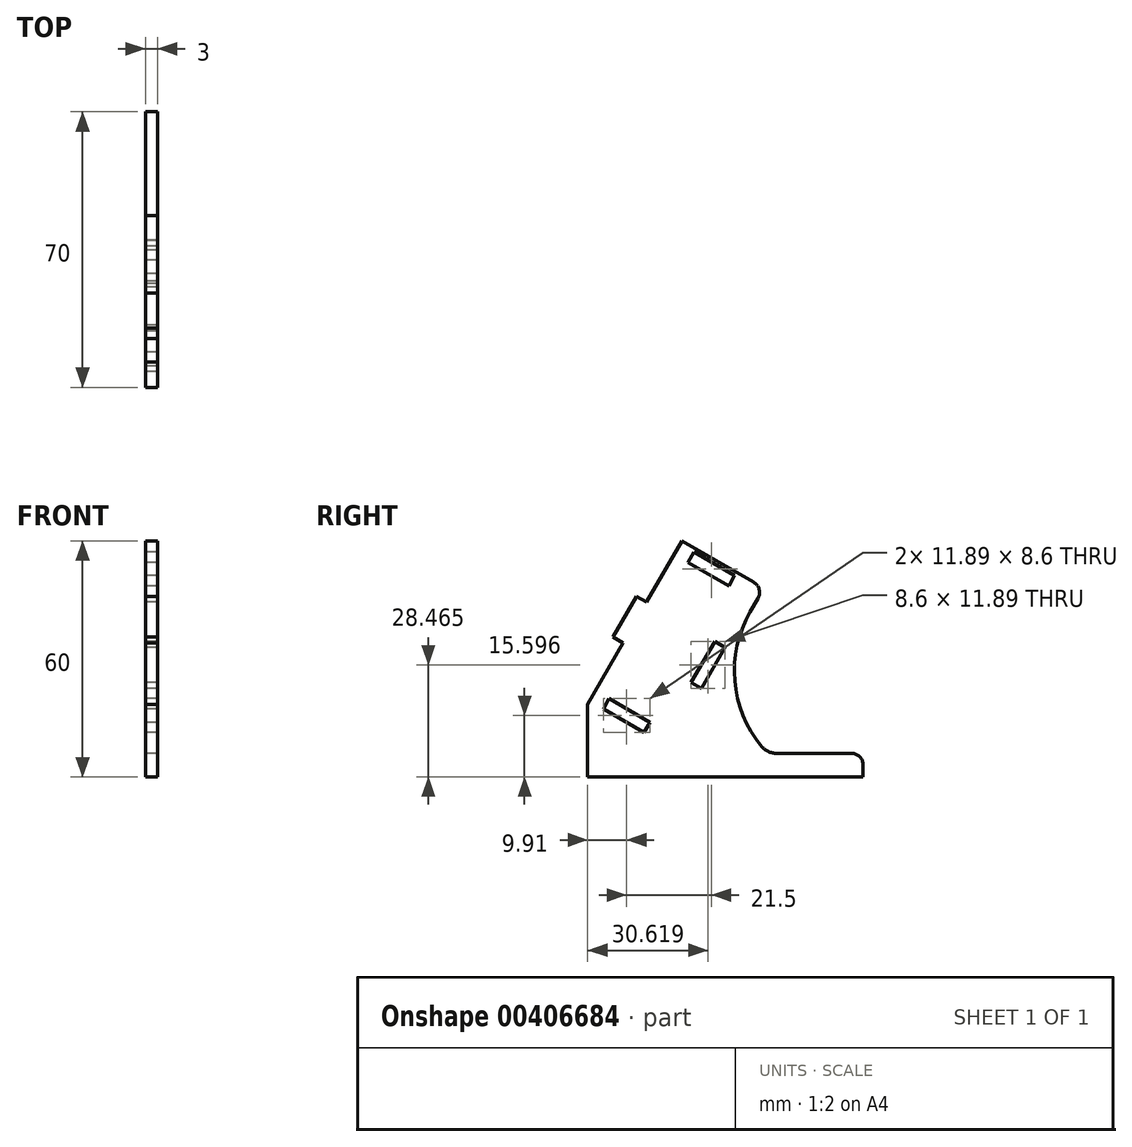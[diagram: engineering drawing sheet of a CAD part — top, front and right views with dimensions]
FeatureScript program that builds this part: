
annotation { "Feature Type Name" : "Feature", "Feature Type Description" : "" }
export const myFeature = defineFeature(function(context is Context, id is Id, definition is map)
    precondition{}
    {
        {
            var Q0;
            Q0=qCreatedBy(makeId("Right.planeOp"),FACE);
            var sketch = newSketch(context, id + "F0", { "sketchPlane" : qUnion([Q0])});
            skLineSegment(sketch, "E0", {"start": v(0, 18.43) * mm, "end": v(9, 34.02) * mm});
            skLineSegment(sketch, "E1", {"start": v(9, 34.02) * mm, "end": v(6.4, 35.52) * mm});
            skLineSegment(sketch, "E2", {"start": v(6.4, 35.52) * mm, "end": v(12.4, 45.91) * mm});
            skLineSegment(sketch, "E3", {"start": v(12.4, 45.91) * mm, "end": v(15, 44.41) * mm});
            skLineSegment(sketch, "E4", {"start": v(15, 44.41) * mm, "end": v(24, 60) * mm});
            skLineSegment(sketch, "E5", {"start": v(24, 60) * mm, "end": v(42.19, 49.5) * mm});
            skLineSegment(sketch, "E6", {"start": v(70, 0) * mm, "end": v(0, 0) * mm});
            skLineSegment(sketch, "E7", {"start": v(26.96, 57.13) * mm, "end": v(25.46, 54.54) * mm});
            skLineSegment(sketch, "E8", {"start": v(25.46, 54.54) * mm, "end": v(35.86, 48.54) * mm});
            skLineSegment(sketch, "E9", {"start": v(35.86, 48.54) * mm, "end": v(37.36, 51.13) * mm});
            skLineSegment(sketch, "E10", {"start": v(37.36, 51.13) * mm, "end": v(26.96, 57.13) * mm});
            skLineSegment(sketch, "E11", {"start": v(9.4, 40.72) * mm, "end": v(18.05, 35.72) * mm, "construction": true});
            skLineSegment(sketch, "E12.MirrorCS", {"start": v(5.46, 19.9) * mm, "end": v(15.86, 13.9) * mm});
            skLineSegment(sketch, "E13.MirrorCS", {"start": v(3.96, 17.3) * mm, "end": v(5.46, 19.9) * mm});
            skLineSegment(sketch, "E14.MirrorCS", {"start": v(14.36, 11.3) * mm, "end": v(3.96, 17.3) * mm});
            skLineSegment(sketch, "E15.MirrorCS", {"start": v(15.86, 13.9) * mm, "end": v(14.36, 11.3) * mm});
            skLineSegment(sketch, "E16", {"start": v(32.32, 34.41) * mm, "end": v(26.32, 24.02) * mm});
            skLineSegment(sketch, "E17", {"start": v(26.32, 24.02) * mm, "end": v(28.92, 22.52) * mm});
            skLineSegment(sketch, "E18", {"start": v(28.92, 22.52) * mm, "end": v(34.92, 32.91) * mm});
            skLineSegment(sketch, "E19", {"start": v(34.92, 32.91) * mm, "end": v(32.32, 34.41) * mm});
            skLineSegment(sketch, "E20", {"start": v(43.28, 45.4) * mm, "end": v(41.28, 41.94) * mm});
            skLineSegment(sketch, "E21", {"start": v(48, 6) * mm, "end": v(67, 6) * mm});
            skLineSegment(sketch, "E22", {"start": v(70, 3) * mm, "end": v(70, 0) * mm});
            skPoint(sketch, "E23.visualSharp", {"position": v(37.25, 6) * mm});
            skArc(sketch, "E23.filletArc", {"start": v(44.15, 7.81) * mm, "mid": v(45.88, 6.48) * mm, "end": v(48, 6) * mm});
            skPoint(sketch, "E24.visualSharp", {"position": v(31.6, 25.17) * mm});
            skArc(sketch, "E24.filletArc", {"start": v(41.28, 41.94) * mm, "mid": v(37.37, 24.43) * mm, "end": v(44.15, 7.81) * mm});
            skPoint(sketch, "E25.visualSharp", {"position": v(70, 6) * mm});
            skArc(sketch, "E25.filletArc", {"start": v(70, 3) * mm, "mid": v(69.12, 5.12) * mm, "end": v(67, 6) * mm});
            skPoint(sketch, "E26.visualSharp", {"position": v(44.78, 48) * mm});
            skArc(sketch, "E26.filletArc", {"start": v(43.28, 45.4) * mm, "mid": v(43.58, 47.68) * mm, "end": v(42.19, 49.5) * mm});
            skLineSegment(sketch, "E27", {"start": v(0, 0) * mm, "end": v(0, 18.43) * mm});
            skLineSegment(sketch, "E28", {"start": v(28.92, 22.52) * mm, "end": v(19.34, 5.93) * mm, "construction": true});
            skLineSegment(sketch, "E29", {"start": v(14.36, 11.3) * mm, "end": v(27.05, 3.97) * mm, "construction": true});
            skLineSegment(sketch, "E30", {"start": v(41.28, 41.94) * mm, "end": v(27.08, 17.33) * mm, "construction": true});
            skSolve(sketch);
        }
        {
            var Q0;
            Q0=makeQuery(id+"F0.imprint","IMPRINT",FACE,{"disambiguationData":[TD([[makeQuery(id+"F0.imprint","IMPRINT",EDGE,{"derivedFrom":sQuery(id+"F0.wireOp",EDGE,"E0")}),-1.0]])]});
            extrude(context, id + "F1", {"entities" : qUnion([Q0]), "depth" : 3 * mm});
        }
    });
